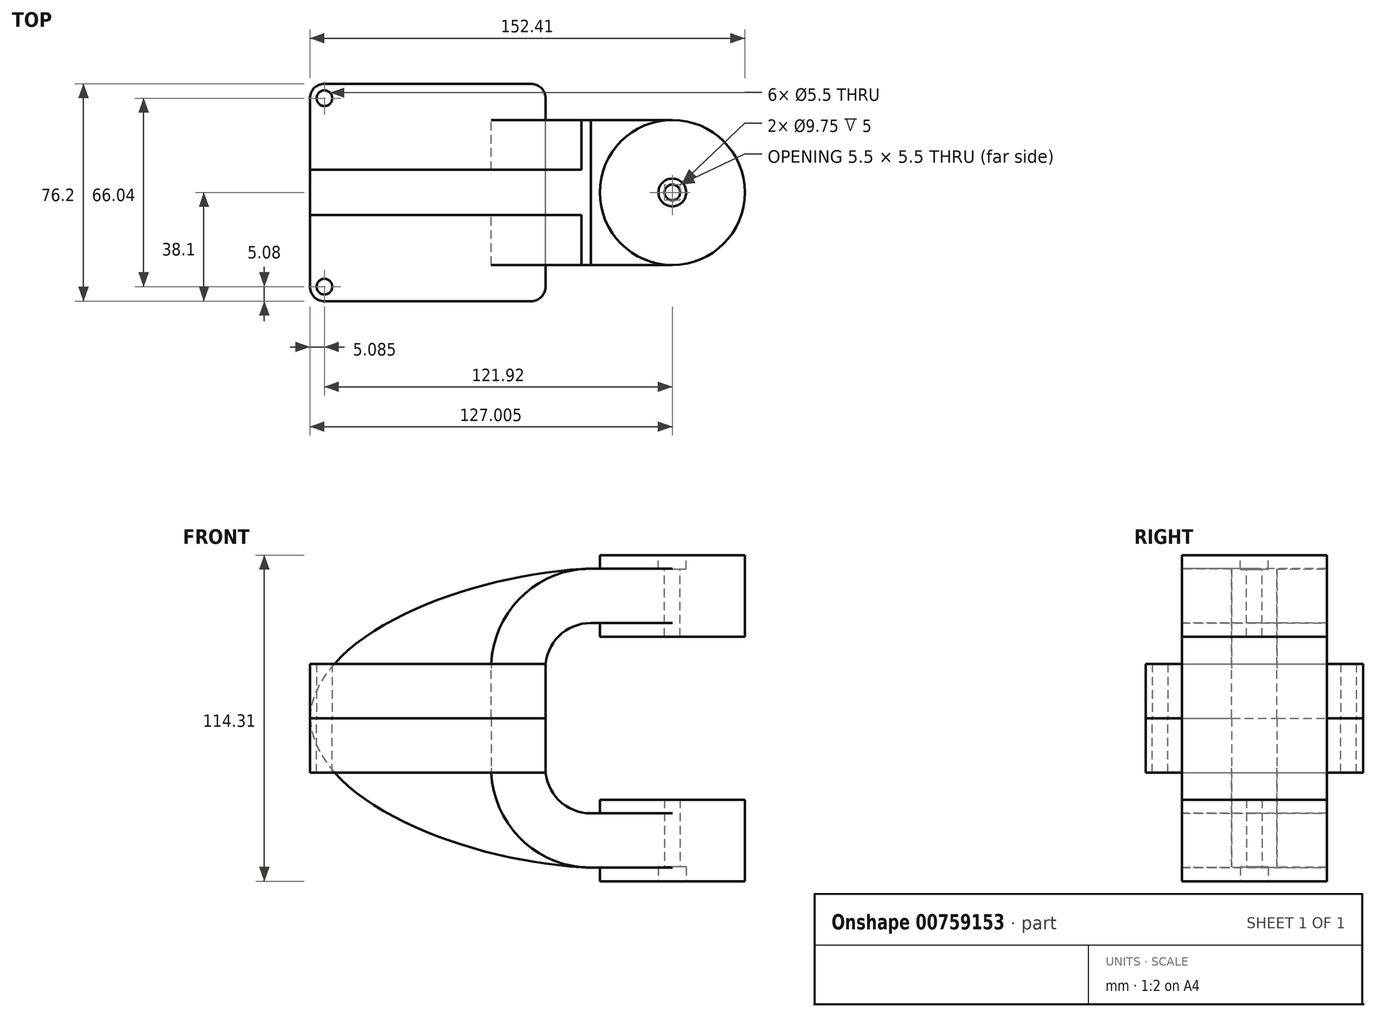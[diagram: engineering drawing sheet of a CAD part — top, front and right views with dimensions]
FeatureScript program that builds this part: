
annotation { "Feature Type Name" : "Feature", "Feature Type Description" : "" }
export const myFeature = defineFeature(function(context is Context, id is Id, definition is map)
    precondition{}
    {
        {
            var Q0;
            Q0=qCreatedBy(makeId("Front.planeOp"),FACE);
            var sketch = newSketch(context, id + "F0", { "sketchPlane" : qUnion([Q0])});
            skLineSegment(sketch, "E0.rect.bottom", {"start": v(-41.28, 9.52) * mm, "end": v(41.28, 9.52) * mm});
            skLineSegment(sketch, "E0.rect.top", {"start": v(-41.28, -9.52) * mm, "end": v(41.28, -9.52) * mm});
            skLineSegment(sketch, "E0.rect.left", {"start": v(-41.28, 9.52) * mm, "end": v(-41.28, -9.52) * mm});
            skLineSegment(sketch, "E0.rect.right", {"start": v(41.28, 9.52) * mm, "end": v(41.28, -9.52) * mm});
            skPoint(sketch, "E0.rect.middle", {"position": v(0, 0) * mm});
            skLineSegment(sketch, "E1", {"start": v(41.28, 9.52) * mm, "end": v(41.28, 27) * mm});
            skArc(sketch, "E2", {"start": v(41.28, 27) * mm, "mid": v(45.92, 38.23) * mm, "end": v(57.15, 42.88) * mm});
            skLineSegment(sketch, "E3", {"start": v(57.15, 42.88) * mm, "end": v(85.72, 42.88) * mm});
            skLineSegment(sketch, "E4.rect.bottom", {"start": v(60.32, 38.1) * mm, "end": v(111.12, 38.1) * mm});
            skLineSegment(sketch, "E4.rect.top", {"start": v(60.32, 66.68) * mm, "end": v(111.12, 66.68) * mm});
            skLineSegment(sketch, "E4.rect.left", {"start": v(60.32, 38.1) * mm, "end": v(60.32, 66.68) * mm});
            skLineSegment(sketch, "E4.rect.right", {"start": v(111.13, 38.1) * mm, "end": v(111.12, 66.68) * mm});
            skPoint(sketch, "E4.rect.middle", {"position": v(85.72, 52.39) * mm});
            skLineSegment(sketch, "E5.0", {"start": v(57.15, 61.93) * mm, "end": v(85.72, 61.93) * mm});
            skArc(sketch, "E5.1", {"start": v(22.23, 27) * mm, "mid": v(32.45, 51.7) * mm, "end": v(57.15, 61.93) * mm});
            skLineSegment(sketch, "E5.2", {"start": v(22.23, 9.52) * mm, "end": v(22.23, 27) * mm});
            skLineSegment(sketch, "E6", {"start": v(85.72, 38.1) * mm, "end": v(85.72, 66.68) * mm});
            skFitSpline(sketch, "E7", {"points": [v(-41.28, 9.53) * mm, v(57.15, 61.93) * mm], "startDerivative": vector(5.2, 92.34) * mm, "endDerivative": vector(120.92, 4.22) * mm});
            skSolve(sketch);
        }
        {
            var Q0;
            Q0=makeQuery(id+"F0.imprint","IMPRINT",FACE,{"disambiguationData":[TD([[makeQuery(id+"F0.imprint","IMPRINT",EDGE,{"derivedFrom":sQuery(id+"F0.wireOp",EDGE,"E0.rect.top")}),1.0]])]});
            extrude(context, id + "F1", {"entities" : qUnion([Q0]), "endBound" : BoundingType.SYMMETRIC, "depth" : 76.2 * mm, "offsetDistance" : 25.4 * mm});
        }
        {
            var Q0;
            {var subQ9=sQuery(id+"F0.wireOp",EDGE,"E1");Q0=makeQuery(id+"F0.imprint","IMPRINT",FACE,{"disambiguationData":[TD([[makeQuery(id+"F0.imprint","IMPRINT",EDGE,{"derivedFrom":subQ9}),1.0]])]});}
            var Q1;
            {var subQ0=sQuery(id+"F0.wireOp",EDGE,"E6");var subQ1=sQuery(id+"F0.wireOp",EDGE,"E3");var subQ2=makeQuery(id+"F0.imprint","INTERSECT",VERTEX,{"derivedFrom":[subQ1,subQ0]});Q1=makeQuery(id+"F0.imprint","IMPRINT",FACE,{"disambiguationData":[TD([[makeQuery(id+"F0.imprint","IMPRINT",EDGE,{"disambiguationData":[TD([[subQ2,1.0]])],"derivedFrom":subQ1}),1.0]])]});}
            extrude(context, id + "F2", {"entities" : qUnion([Q0, Q1]), "operationType" : NewBodyOperationType.ADD, "endBound" : BoundingType.SYMMETRIC, "depth" : 50.8 * mm});
        }
        {
            var Q0;
            {var subQ3=sQuery(id+"F0.wireOp",EDGE,"E5.2");Q0=makeQuery(id+"F0.imprint","IMPRINT",FACE,{"disambiguationData":[TD([[makeQuery(id+"F0.imprint","IMPRINT",EDGE,{"derivedFrom":subQ3}),1.0]])]});}
            extrude(context, id + "F3", {"entities" : qUnion([Q0]), "operationType" : NewBodyOperationType.ADD, "endBound" : BoundingType.SYMMETRIC, "depth" : 15.88 * mm});
        }
        {
            var Q0;
            {var subQ5=sQuery(id+"F0.wireOp",EDGE,"E4.rect.right");Q0=makeQuery(id+"F0.imprint","IMPRINT",FACE,{"disambiguationData":[TD([[makeQuery(id+"F0.imprint","IMPRINT",EDGE,{"derivedFrom":subQ5}),1.0]])]});}
            var Q1;
            Q1=sQuery(id+"F0.wireOp",EDGE,"E6");
            revolve(context, id + "F4", {"operationType" : NewBodyOperationType.ADD, "entities" : qUnion([Q0]), "axis" : qUnion([Q1]), "revolveType" : RevolveType.FULL});
        }
        {
            var Q0;
            Q0=makeQuery(id+"F1.opExtrude","CAP_EDGE",EDGE,{"disambiguationData":[OSD([sQuery(id+"F0.wireOp",EDGE,"E0.rect.right")])],"isStart":false});
            var Q1;
            Q1=makeQuery(id+"F1.opExtrude","CAP_EDGE",EDGE,{"disambiguationData":[OSD([sQuery(id+"F0.wireOp",EDGE,"E0.rect.left")])],"isStart":false});
            var Q2;
            Q2=makeQuery(id+"F1.opExtrude","CAP_EDGE",EDGE,{"disambiguationData":[OSD([sQuery(id+"F0.wireOp",EDGE,"E0.rect.right")])],"isStart":true});
            var Q3;
            Q3=makeQuery(id+"F1.opExtrude","CAP_EDGE",EDGE,{"disambiguationData":[OSD([sQuery(id+"F0.wireOp",EDGE,"E0.rect.left")])],"isStart":true});
            fillet(context, id + "F5", {"entities" : qUnion([Q0, Q1, Q2, Q3]), "radius" : 5.08 * mm, "tangentPropagation" : true, "allowEdgeOverflow" : false});
        }
        {
            var Q0;
            Q0=makeQuery(id+"F4.opRevolve","SWEPT_FACE",FACE,{"disambiguationData":[OSD([sQuery(id+"F0.wireOp",EDGE,"E4.rect.top")])]});
            var sketch = newSketch(context, id + "F6", { "sketchPlane" : qUnion([Q0])});
            skCircle(sketch, "E8", {"center": v(85.72, 0) * mm, "radius": 10.42 * mm});
            skSolve(sketch);
        }
        {
            var Q0;
            {var subQ4=sQuery(id+"F0.wireOp",EDGE,"E0.rect.bottom");var subQ5=sQuery(id+"F0.wireOp",EDGE,"E0.rect.right");var subQ6=sQuery(id+"F0.wireOp",EDGE,"E0.rect.left");Q0=makeQuery(id+"F3.boolean.opBoolean","SPLIT",FACE,{"disambiguationData":[TD([makeQuery(id+"F1.opExtrude","CAP_FACE",FACE,{"disambiguationData":[OSD([subQ4,sQuery(id+"F0.wireOp",EDGE,"E0.rect.top"),subQ6,subQ5])],"isStart":true})])],"derivedFrom":makeQuery(id+"F1.opExtrude","SWEPT_FACE",FACE,{"disambiguationData":[OSD([subQ4])]})});}
            var sketch = newSketch(context, id + "F7", { "sketchPlane" : qUnion([Q0])});
            skCircle(sketch, "E9", {"center": v(-36.2, 33.02) * mm, "radius": 3.55 * mm});
            skSolve(sketch);
        }
        {
            var Q0;
            Q0=sQuery(id+"F6.wireOp",VERTEX,"E8.center");
            var Q1;
            Q1=makeQuery(id+"F1.opExtrude","SWEPT_BODY",BODY,{"disambiguationData":[OSD([sQuery(id+"F0.wireOp",EDGE,"E0.rect.bottom"),sQuery(id+"F0.wireOp",EDGE,"E0.rect.top"),sQuery(id+"F0.wireOp",EDGE,"E0.rect.left"),sQuery(id+"F0.wireOp",EDGE,"E0.rect.right")])]});
            hole(context, id + "F8", {"style" : HoleStyle.C_BORE, "endStyle" : HoleEndStyle.THROUGH, "standardTappedOrClearance" : lookupTablePath({ "standard" : "ISO", "fit" : "Normal", "size" : "M5", "type" : "Clearance" }), "standardBlindInLast" : lookupTablePath({ "fit" : "Standard", "standard" : "ISO", "size" : "M5", "type" : "Clearance" }), "holeDiameter" : 5.5 * mm, "cBoreDiameter" : 9.75 * mm, "cBoreDepth" : 5 * mm, "majorDiameter" : 6.35 * mm, "isTappedThrough" : true, "tappedDepth" : 12.7 * mm, "tapClearance" : 3, "startFromSketch" : true, "locations" : qUnion([Q0]), "scope" : qUnion([Q1])});
        }
        {
            var Q0;
            Q0=sQuery(id+"F7.wireOp",VERTEX,"E9.center");
            var Q1;
            Q1=makeQuery(id+"F1.opExtrude","SWEPT_BODY",BODY,{"disambiguationData":[OSD([sQuery(id+"F0.wireOp",EDGE,"E0.rect.bottom"),sQuery(id+"F0.wireOp",EDGE,"E0.rect.top"),sQuery(id+"F0.wireOp",EDGE,"E0.rect.left"),sQuery(id+"F0.wireOp",EDGE,"E0.rect.right")])]});
            hole(context, id + "F9", {"style" : HoleStyle.SIMPLE, "endStyle" : HoleEndStyle.THROUGH, "standardTappedOrClearance" : lookupTablePath({ "standard" : "ISO", "fit" : "Normal", "size" : "M5", "type" : "Clearance" }), "standardBlindInLast" : lookupTablePath({ "fit" : "Standard", "standard" : "ISO", "size" : "M5", "type" : "Clearance" }), "holeDiameter" : 5.5 * mm, "majorDiameter" : 6.35 * mm, "isTappedThrough" : true, "tappedDepth" : 12.7 * mm, "tapClearance" : 3, "startFromSketch" : true, "locations" : qUnion([Q0]), "scope" : qUnion([Q1])});
        }
        {
            var Q0;
            {var subQ4=sQuery(id+"F0.wireOp",EDGE,"E0.rect.bottom");var subQ5=sQuery(id+"F0.wireOp",EDGE,"E0.rect.right");var subQ6=sQuery(id+"F0.wireOp",EDGE,"E0.rect.left");Q0=makeQuery(id+"F3.boolean.opBoolean","SPLIT",FACE,{"disambiguationData":[TD([makeQuery(id+"F1.opExtrude","CAP_FACE",FACE,{"disambiguationData":[OSD([subQ4,sQuery(id+"F0.wireOp",EDGE,"E0.rect.top"),subQ6,subQ5])],"isStart":false})])],"derivedFrom":makeQuery(id+"F1.opExtrude","SWEPT_FACE",FACE,{"disambiguationData":[OSD([subQ4])]})});}
            var sketch = newSketch(context, id + "F10", { "sketchPlane" : qUnion([Q0])});
            skCircle(sketch, "E10", {"center": v(-36.2, -33.02) * mm, "radius": 3.33 * mm});
            skSolve(sketch);
        }
        {
            var Q0;
            Q0=sQuery(id+"F10.wireOp",VERTEX,"E10.center");
            var Q1;
            Q1=makeQuery(id+"F1.opExtrude","SWEPT_BODY",BODY,{"disambiguationData":[OSD([sQuery(id+"F0.wireOp",EDGE,"E0.rect.bottom"),sQuery(id+"F0.wireOp",EDGE,"E0.rect.top"),sQuery(id+"F0.wireOp",EDGE,"E0.rect.left"),sQuery(id+"F0.wireOp",EDGE,"E0.rect.right")])]});
            hole(context, id + "F11", {"style" : HoleStyle.SIMPLE, "endStyle" : HoleEndStyle.THROUGH, "standardTappedOrClearance" : lookupTablePath({ "standard" : "ISO", "fit" : "Normal", "size" : "M5", "type" : "Clearance" }), "standardBlindInLast" : lookupTablePath({ "fit" : "Standard", "standard" : "ISO", "size" : "M5", "type" : "Clearance" }), "holeDiameter" : 5.5 * mm, "majorDiameter" : 6.35 * mm, "isTappedThrough" : true, "tappedDepth" : 12.7 * mm, "tapClearance" : 3, "startFromSketch" : true, "locations" : qUnion([Q0]), "scope" : qUnion([Q1])});
        }
        {
            var Q0;
            Q0=makeQuery(id+"F1.opExtrude","SWEPT_BODY",BODY,{"disambiguationData":[OSD([sQuery(id+"F0.wireOp",EDGE,"E0.rect.bottom"),sQuery(id+"F0.wireOp",EDGE,"E0.rect.top"),sQuery(id+"F0.wireOp",EDGE,"E0.rect.left"),sQuery(id+"F0.wireOp",EDGE,"E0.rect.right")])]});
            var Q1;
            {var subQ4=sQuery(id+"F0.wireOp",EDGE,"E0.rect.bottom");var subQ5=sQuery(id+"F0.wireOp",EDGE,"E0.rect.right");var subQ6=sQuery(id+"F0.wireOp",EDGE,"E0.rect.left");Q1=makeQuery(id+"F3.boolean.opBoolean","SPLIT",FACE,{"disambiguationData":[TD([makeQuery(id+"F1.opExtrude","CAP_FACE",FACE,{"disambiguationData":[OSD([subQ4,sQuery(id+"F0.wireOp",EDGE,"E0.rect.top"),subQ6,subQ5])],"isStart":true})])],"derivedFrom":makeQuery(id+"F1.opExtrude","SWEPT_FACE",FACE,{"disambiguationData":[OSD([subQ4])]})});}
            mirror(context, id + "F12", {"entities" : qUnion([Q0]), "mirrorPlane" : qUnion([Q1])});
        }
    });
